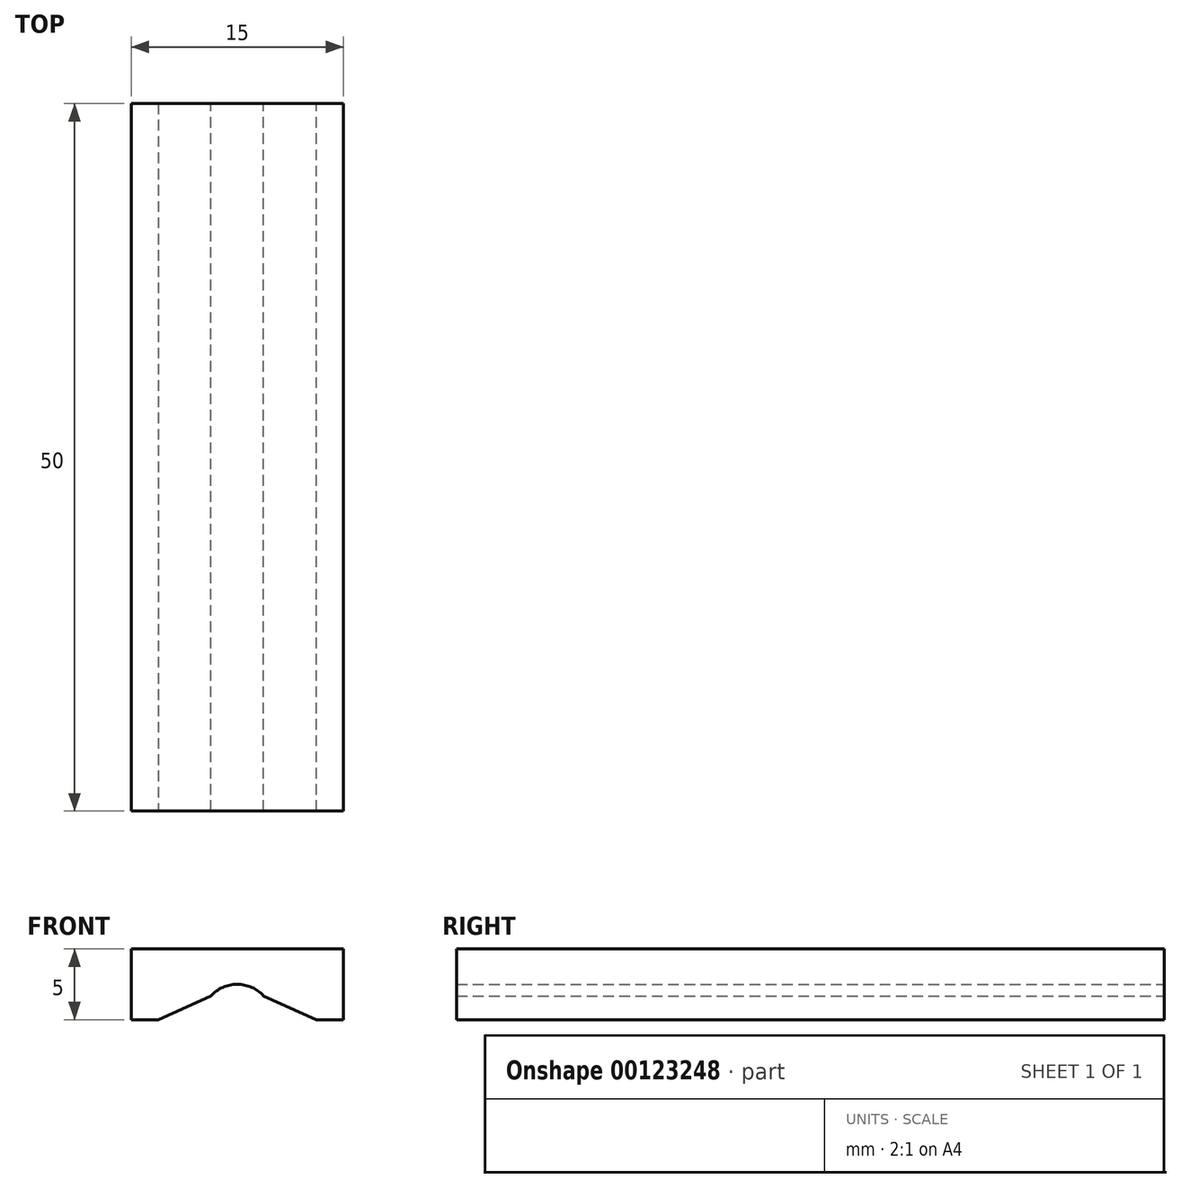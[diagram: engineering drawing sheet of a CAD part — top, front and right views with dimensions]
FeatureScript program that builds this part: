
annotation { "Feature Type Name" : "Feature", "Feature Type Description" : "" }
export const myFeature = defineFeature(function(context is Context, id is Id, definition is map)
    precondition{}
    {
        {
            var Q0;
            Q0=qCreatedBy(makeId("Front.planeOp"),FACE);
            var sketch = newSketch(context, id + "F0", { "sketchPlane" : qUnion([Q0])});
            skLineSegment(sketch, "E0", {"start": v(0, 5) * mm, "end": v(7.5, 5) * mm});
            skLineSegment(sketch, "E1", {"start": v(7.5, 5) * mm, "end": v(7.5, 0) * mm});
            skLineSegment(sketch, "E2", {"start": v(7.5, 0) * mm, "end": v(2.5, 0) * mm});
            skArc(sketch, "E3", {"start": v(2.5, 0) * mm, "mid": v(1.77, 1.77) * mm, "end": v(0, 2.5) * mm});
            skLineSegment(sketch, "E4.MirrorCS", {"start": v(0, 5) * mm, "end": v(-7.5, 5) * mm});
            skLineSegment(sketch, "E5.MirrorCS", {"start": v(-7.5, 5) * mm, "end": v(-7.5, 0) * mm});
            skLineSegment(sketch, "E6.MirrorCS", {"start": v(-7.5, 0) * mm, "end": v(-2.5, 0) * mm});
            skArc(sketch, "E7.MirrorCS", {"start": v(-2.5, 0) * mm, "mid": v(-1.77, 1.77) * mm, "end": v(0, 2.5) * mm});
            skSolve(sketch);
        }
        {
            var Q0;
            Q0 = qSketchRegion(id + "F0", true);
            extrude(context, id + "F1", {"entities" : qUnion([Q0]), "depth" : 50 * mm});
        }
        {
            var Q0;
            Q0=makeQuery(id+"F1.opExtrude","SWEPT_EDGE",EDGE,{"disambiguationData":[OSD([sQuery(id+"F0.wireOp",EDGE,"E6.MirrorCS"),sQuery(id+"F0.wireOp",EDGE,"E7.MirrorCS")])]});
            var Q1;
            Q1=makeQuery(id+"F1.opExtrude","SWEPT_EDGE",EDGE,{"disambiguationData":[OSD([sQuery(id+"F0.wireOp",EDGE,"E2"),sQuery(id+"F0.wireOp",EDGE,"E3")])]});
            chamfer(context, id + "F2", {"entities" : qUnion([Q0, Q1]), "width" : 5 * mm, "tangentPropagation" : true});
        }
    });
